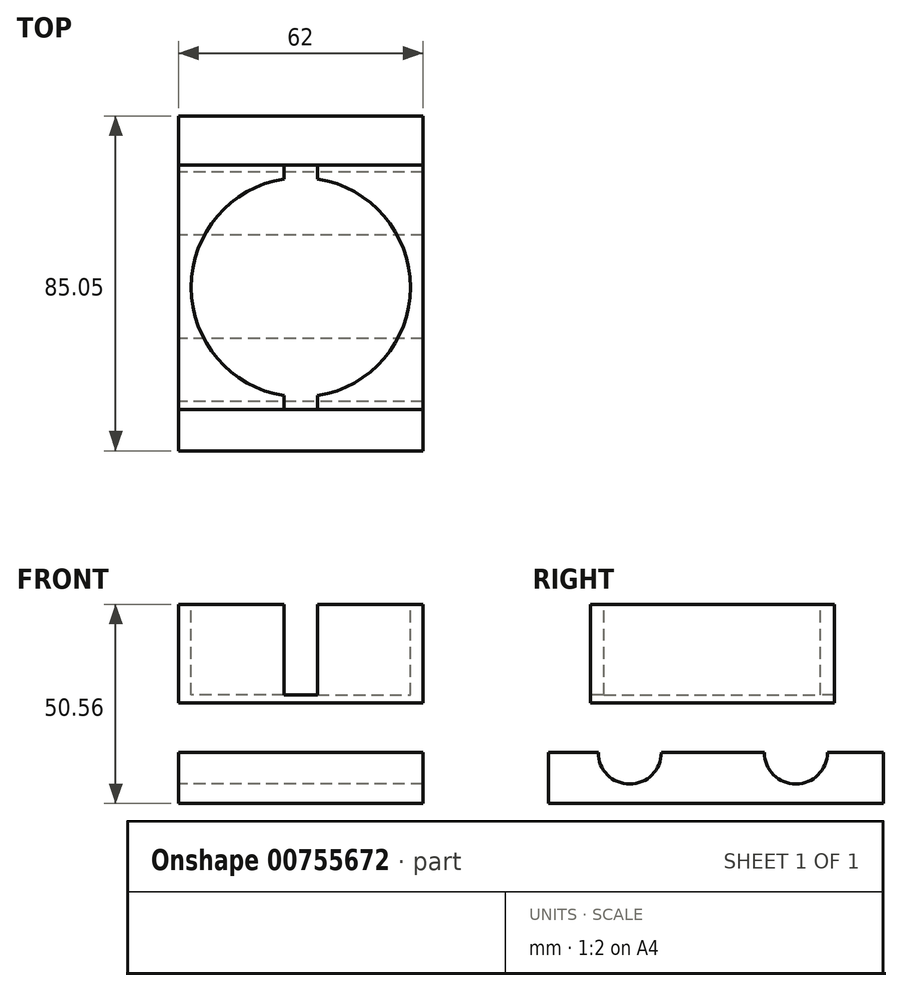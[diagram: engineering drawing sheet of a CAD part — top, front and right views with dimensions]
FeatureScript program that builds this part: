
annotation { "Feature Type Name" : "Feature", "Feature Type Description" : "" }
export const myFeature = defineFeature(function(context is Context, id is Id, definition is map)
    precondition{}
    {
        {
            var Q0;
            Q0=qCreatedBy(makeId("Top.planeOp"),FACE);
            var sketch = newSketch(context, id + "F0", { "sketchPlane" : qUnion([Q0])});
            skLineSegment(sketch, "E0.bottom", {"start": v(31, -31) * mm, "end": v(-31, -31) * mm});
            skLineSegment(sketch, "E0.top", {"start": v(31, 31) * mm, "end": v(-31, 31) * mm});
            skLineSegment(sketch, "E0.left", {"start": v(31, -31) * mm, "end": v(31, 31) * mm});
            skLineSegment(sketch, "E0.right", {"start": v(-31, -31) * mm, "end": v(-31, 31) * mm});
            skPoint(sketch, "E0.middle", {"position": v(0, 0) * mm});
            skSolve(sketch);
        }
        {
            var Q0;
            Q0=makeQuery(id+"F0.imprint","IMPRINT",FACE,{"disambiguationData":[TD([[makeQuery(id+"F0.imprint","IMPRINT",EDGE,{"derivedFrom":sQuery(id+"F0.wireOp",EDGE,"E0.bottom")}),-1.0]])]});
            extrude(context, id + "F1", {"entities" : qUnion([Q0]), "endBound" : BoundingType.SYMMETRIC, "depth" : 25 * mm, "offsetDistance" : 25 * mm});
        }
        {
            var Q0;
            Q0=makeQuery(id+"F1.opExtrude","CAP_FACE",FACE,{"disambiguationData":[OSD([sQuery(id+"F0.wireOp",EDGE,"E0.bottom"),sQuery(id+"F0.wireOp",EDGE,"E0.top"),sQuery(id+"F0.wireOp",EDGE,"E0.left"),sQuery(id+"F0.wireOp",EDGE,"E0.right")])],"isStart":false});
            var sketch = newSketch(context, id + "F2", { "sketchPlane" : qUnion([Q0])});
            skCircle(sketch, "E1", {"center": v(0, 0) * mm, "radius": 27.85 * mm});
            skSolve(sketch);
        }
        {
            var Q0;
            Q0=makeQuery(id+"F2.imprint","IMPRINT",FACE,{"disambiguationData":[TD([[makeQuery(id+"F2.imprint","IMPRINT",EDGE,{"derivedFrom":sQuery(id+"F2.wireOp",EDGE,"E1")}),1.0]])]});
            extrude(context, id + "F3", {"entities" : qUnion([Q0]), "operationType" : NewBodyOperationType.REMOVE, "oppositeDirection" : true, "depth" : 23 * mm, "offsetDistance" : 25 * mm});
        }
        {
            var Q0;
            Q0=makeQuery(id+"F1.opExtrude","SWEPT_FACE",FACE,{"disambiguationData":[OSD([sQuery(id+"F0.wireOp",EDGE,"E0.bottom")])]});
            var sketch = newSketch(context, id + "F4", { "sketchPlane" : qUnion([Q0])});
            skLineSegment(sketch, "E2.bottom", {"start": v(-4.25, 12.5) * mm, "end": v(4.25, 12.5) * mm});
            skLineSegment(sketch, "E2.left", {"start": v(-4.25, 12.5) * mm, "end": v(-4.25, -12.5) * mm});
            skLineSegment(sketch, "E2.right", {"start": v(4.25, 12.5) * mm, "end": v(4.25, -12.5) * mm});
            skPoint(sketch, "E2.middle", {"position": v(0, 0) * mm});
            skLineSegment(sketch, "E3", {"start": v(-4.25, -10.5) * mm, "end": v(4.25, -10.5) * mm});
            skSolve(sketch);
        }
        {
            var Q0;
            {var subQ0=sQuery(id+"F4.wireOp",EDGE,"E2.bottom");Q0=makeQuery(id+"F4.imprint","IMPRINT",FACE,{"disambiguationData":[TD([[makeQuery(id+"F4.imprint","IMPRINT",EDGE,{"derivedFrom":subQ0}),1.0]])]});}
            extrude(context, id + "F5", {"entities" : qUnion([Q0]), "operationType" : NewBodyOperationType.REMOVE, "oppositeDirection" : true, "depth" : 72.3 * mm, "offsetDistance" : 25 * mm});
        }
        {
            var Q0;
            Q0=qCreatedBy(makeId("Right.planeOp"),FACE);
            var sketch = newSketch(context, id + "F6", { "sketchPlane" : qUnion([Q0])});
            skLineSegment(sketch, "E4", {"start": v(-41.56, -25.15) * mm, "end": v(-41.56, -38.06) * mm});
            skLineSegment(sketch, "E5", {"start": v(-41.56, -38.06) * mm, "end": v(43.49, -38.06) * mm});
            skLineSegment(sketch, "E6", {"start": v(43.49, -25.15) * mm, "end": v(43.49, -38.06) * mm});
            skLineSegment(sketch, "E7", {"start": v(-41.56, -25.15) * mm, "end": v(-28.98, -25.15) * mm});
            skArc(sketch, "E8", {"start": v(-28.98, -25.15) * mm, "mid": v(-20.98, -33.15) * mm, "end": v(-12.98, -25.15) * mm});
            skArc(sketch, "E9.1.0.0", {"start": v(13.23, -25.15) * mm, "mid": v(21.23, -33.15) * mm, "end": v(29.23, -25.15) * mm});
            skLineSegment(sketch, "E10", {"start": v(29.23, -25.15) * mm, "end": v(43.49, -25.15) * mm});
            skLineSegment(sketch, "E11", {"start": v(-12.98, -25.15) * mm, "end": v(13.23, -25.15) * mm});
            skLineSegment(sketch, "E12", {"start": v(-20.98, -33.15) * mm, "end": v(21.23, -33.15) * mm, "construction": true});
            skPoint(sketch, "E12.endSnap0", {"position": v(21.23, -33.15) * mm});
            skSolve(sketch);
        }
        {
            var Q0;
            Q0=makeQuery(id+"F6.imprint","IMPRINT",FACE,{"disambiguationData":[TD([[makeQuery(id+"F6.imprint","IMPRINT",EDGE,{"derivedFrom":sQuery(id+"F6.wireOp",EDGE,"E4")}),1.0]])]});
            var Q1;
            Q1=makeQuery(id+"F1.opExtrude","SWEPT_FACE",FACE,{"disambiguationData":[OSD([sQuery(id+"F0.wireOp",EDGE,"E0.left")])]});
            var Q2;
            Q2=makeQuery(id+"F1.opExtrude","SWEPT_FACE",FACE,{"disambiguationData":[OSD([sQuery(id+"F0.wireOp",EDGE,"E0.right")])]});
            extrude(context, id + "F7", {"entities" : qUnion([Q0]), "endBound" : BoundingType.UP_TO_SURFACE, "depth" : 58.6 * mm, "endBoundEntityFace" : qUnion([Q1]), "offsetDistance" : 25 * mm, "hasSecondDirection" : true, "secondDirectionBound" : SecondDirectionBoundingType.UP_TO_SURFACE, "secondDirectionOppositeDirection" : true, "secondDirectionDepth" : 25 * mm, "secondDirectionBoundEntityFace" : qUnion([Q2])});
        }
    });
